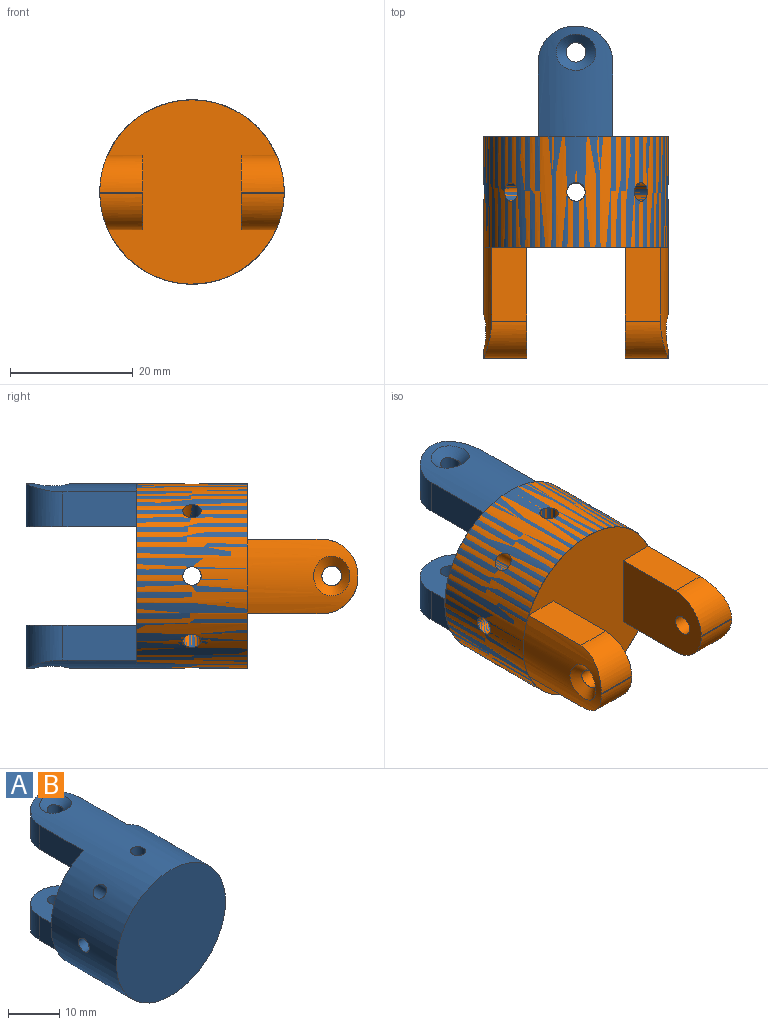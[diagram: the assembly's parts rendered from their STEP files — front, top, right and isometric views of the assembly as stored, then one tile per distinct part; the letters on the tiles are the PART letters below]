
ASSEMBLY  parts=2 mates=1
PART A: 27 faces, bbox 30x36x30 mm
  f0: plane 12x5.75mm, normal (1,0,0), area 69mm2, adj f4,f6,f12,f16
  f1: plane 12x5.68mm, normal (-1,0,0), area 68.1mm2, adj f4,f6,f12,f17
  f2: cylinder r=1.5mm len=14.93mm, axis (1,0,0), area 121.3mm2, adj f4,f23,f26
  f3: plane 7x0.16mm, normal (0,1,0), area 1.1mm2, adj f4,f7,f14,f15
  f4: cylinder r=15mm len=36mm, axis (0,1,0), area 1998mm2, adj f0,f1,f2,f3,f5,f8,f11,f12
  f5: plane 7x0.16mm, normal (0,1,0), area 1.1mm2, adj f4,f6,f16,f17
  f6: plane 18x12.16mm, normal (0,0,1), area 195.5mm2, adj f0,f1,f5,f10,f12,f16,f17
  f7: plane 18x12.16mm, normal (0,0,-1), area 195.5mm2, adj f3,f9,f11,f12,f13,f14,f15
  f8: plane 30x30mm, normal (0,-1,0), area 706.9mm2, adj f4
  f9: cylinder r=1.6mm len=5.65mm, axis (0,0,1), area 56.8mm2, adj f7,f18
  f10: cylinder r=1.6mm len=5.33mm, axis (0,0,1), area 53.6mm2, adj f6,f19
  f11: plane 12x5.75mm, normal (1,0,0), area 69mm2, adj f4,f7,f12,f15
  f12: plane 30x27.5mm, normal (0,1,0), area 546.8mm2, adj f0,f1,f4,f6,f7,f11,f13
  f13: plane 12x5.68mm, normal (-1,0,0), area 68.1mm2, adj f4,f7,f12,f14
  f14: cylinder r=6mm len=7mm, axis (0,0,-1), area 59.7mm2, adj f3,f4,f7,f13
  f15: cylinder r=6mm len=7mm, axis (0,0,1), area 60.1mm2, adj f3,f4,f7,f11
  f16: cylinder r=6mm len=7mm, axis (0,0,1), area 60.1mm2, adj f0,f4,f5,f6
  f17: cylinder r=6mm len=7mm, axis (0,0,-1), area 59.7mm2, adj f1,f4,f5,f6
  f18: bspline ~6.48x5.9mm, area 29.7mm2, adj f4,f9
  f19: bspline ~6.47x5.89mm, area 29.7mm2, adj f4,f10
  f20: cylinder r=1.5mm len=14.93mm, axis (1,0,0), area 121.3mm2, adj f4,f24,f25
  f21: cylinder r=1.5mm len=15mm, axis (0,0,1), area 124.3mm2, adj f4,f24,f26
  f22: cylinder r=1.5mm len=14.93mm, axis (0,0,1), area 121.3mm2, adj f4,f23,f25
  f23: cylinder r=1.5mm len=12.67mm, axis (-0.71,0,0.71), area 123.6mm2, adj f2,f4,f22
  f24: cylinder r=1.5mm len=12.67mm, axis (-0.71,0,0.71), area 121.3mm2, adj f4,f20,f21
  f25: cylinder r=1.5mm len=12.67mm, axis (-0.71,0,-0.71), area 121.3mm2, adj f4,f20,f22
  f26: cylinder r=1.5mm len=12.67mm, axis (-0.71,0,-0.71), area 121.3mm2, adj f2,f4,f21
PART B: same geometry as A
PLACE A t=(-3.18,5.14,-3.04)mm
PLACE B rot(axis=(0.71,0,0.71),180deg) t=(-3.18,-48.86,-3.04)mm
MATE planar B.f4 <-> A.f4  axis (0,1,0) through (-3.18,-12.86,-3.04)mm
